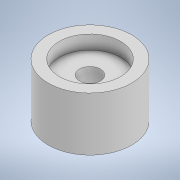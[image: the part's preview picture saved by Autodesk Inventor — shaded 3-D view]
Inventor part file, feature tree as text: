
AUTODESK INVENTOR PART (.ipt)
format: ipt  version: 2020 (Build 240168000, 168)  size: 113,152 bytes
history: native  units: in
note: dims shown in document units (in); Inventor stores cm internally (conversion verified against a paired STEP export)
features: extrude x3, sketch x3
ambient origin geometry x8: Origin, YZ Plane, XZ Plane, XY Plane, X Axis, Y Axis, Z Axis, Center Point
bodies: Solid1 (feature_tree)
feature tree (6):
  extrude  "Extrusion1"  Depth=0.9656in TaperAngle=0.0deg
  extrude  "Extrusion2"  Depth=0.25in TaperAngle=0.0deg
  extrude  "Extrusion3"  Depth=0.7874in TaperAngle=0.0deg
  sketch  "Sketch1"  dims[d0=1.5in d1=0.9656in d2=0.0in]
  sketch  "Sketch2"  dims[d3=1.1in d4=0.25in d5=0.0in]
  sketch  "Sketch3"  dims[d6=0.375in d7=0.7874in d8=0.0in]
